# Revit family: WTC-OB25W-RU20
name_source: partatom
category: HLS-Bauteile
revit_build: Autodesk Revit 2017 (Build: 20160225_1515(x64)
units: mm (PartAtom-declared; Revit-internal decimal feet)

## family parameters
Arbeitsebenenbasiert = Nein
Beim Laden mit Abzugskörper schneiden = Nein
Bemaßung runder Anschluss = Durchmesser verwenden
Gemeinsam genutzt = Nein
Immer vertikal = Ja
Raumberechnungspunkt = Nein
Teiletyp = Normal

## types (1)
- Thermo Condens, WTC-OB 25-A W-PEA, 24.3 kW
    Anordnung, Lage = nebenstehend
    Baugruppenkennzeichen = ????
    Beschreibung = Weishaupt Thermo Condens Ölbrennwert Typ WTC-OB 25-A Ausf. W-PEA
    Bestellnummer = 46211201
    Brennstoffart = flüssige Brennstoffe
    Datanorm Nummer = 46211201
    Generiert am = 06.02.2018
    Generiert durch = Rubicon Professional Solutions GmbH
    Hersteller = MAX WEISHAUPT GMBH
    Herstellerkurzname = Weishaupt
    Modell = Thermo Condens WTC-OB 25-A W-PEA
    Name der Richtlinie = Wärmeerzeuger
    Produktgruppe = Brennwert-Kessel
    Quelle = http://www.vdi3805-portal.de
    Revisionsdatum der VDI-Datei = 09.10.2017
    Stand der Richtlinie = 01.06.2004
    TGA-Nr = 00100100000400000000100000000400200000000000002531???00001000010000100000000000000000001
    Trinkwasserprinzip = Speicher extern
    Typenbezeichnung (Name) = Thermo Condens, WTC-OB 25-A W-PEA, 24.3 kW
    Typenkommentare = Die Daten geben den Stand des eingeblendeten Datums wieder. Fuer Vollstaendigkeit und Richtigkeit kann keine Gewaehr uebernommen werden!
    URL = http://www.weishaupt.de
    VDI3805-Richtlinienblatt = 3
    Web-Adresse = http://www.vdi3805-portal.de
    WebService = http://www.vdi3805-portal.de
    Werkstoff = Aluminium
    XML = <?xml version="1.0"?>
<pData xmlns="http://www.rubicon-professional.de xmlns:xsi="http://www.w3.org filename="PART03_Weishaupt.VDI" shortname="Weishaupt" manufacturername="MAX WEISHAUPT GMBH" tganr="00100100000400000000100000000400200000000000002531???00001000010000100000000000000000001|" language="de-DE"/><REC010 IDX="010" index="3" content="010;3;200406;MAX WEISHAUPT GMBH;20171009;http://www.weishaupt.de;Die Daten geben den Stand des eingeblendeten Datums wieder. Fuer Vollstaendigkeit und Richtigkeit kann keine Gewaehr uebernommen werden!;1234567890123;;;1;20170801;DEU;DE;201110;"><RECORDS_100><REC100 IDX="100" index="1" content="100;1;1;Bodenstehender Waermeerzeuger, nur fuer Heizung;;;20071101;"><RECORDS_110><REC110 IDX="110" index="1" content="110;1;1;mit Geblaese;;;20071101;"><RECORDS_200><REC200 IDX="200" index="4" content="200;4;Aluminium;"/></RECORDS_200><RECORDS_300><REC300 IDX="300" index="1" content="300;1;fluessige Brennstoffe;"/></RECORDS_300><RECORDS_400><REC400 IDX="400" index="4" content="400;4;Speicher extern;"><RECORDS_450><REC450 IDX="450" index="2" content="450;2;nebenstehend;"/></RECORDS_450></REC400></RECORDS_400><RECORDS_700><REC700 IDX="700" index="2531" content="700;2531;23;Thermo Condens;WTC-OB 25-A W-PEA;24.3;140;23;;;;;15.4;3;Brennwert-Kessel;1;2-Zug-Kessel;1.1;3;raumluftabhaengig oder -unabhaengig;1;1;80;125;;;96.2;0.004;0.156;24.3;"><RECORDS_710_01><REC71001 IDX="710.01" index="1" content="710.01;1;40/30;15.8;25.9;105;98;102;85;0;33;;85;;;;;;3;;100;0;;;24;215;1;7;90;17330;63;"><RECORDS_710_11><REC71011 IDX="710.11" index="1" content="710.11;1;1;9;Heizoel EL;"/></RECORDS_710_11></REC71001></RECORDS_710_01><RECORDS_710_05><REC71005 IDX="710.05" index="1" content="710.05;1;2;zweistufig;0.0107;0.0062;;56;54;;13;13;100;10;;;6;Klasse 3/EN 676;;purflam-Oelbrenner;;25.2;"/></RECORDS_710_05><RECORDS_710_10><REC71010 IDX="710.10" index="1" content="710.10;1;2;730;680;1182;Geraetemass;"/><REC71010 IDX="710.10" index="2" content="710.10;2;2;1250;680;1182;Platzbedarf fuer Wartung;"/></RECORDS_710_10><RECORDS_710_12><REC71012 IDX="710.12" index="1" content="710.12;1;6;Aussenfuehler mit modulierendem Volumenstrom;4;1;1;0;1;1;7;0;1;1;1;1;1;Weishaupt Condens Manager WCM;;4;0;"/></RECORDS_710_12><RECORDS_720><REC720 IDX="720" index="1" content="720;1;46201102;"/></RECORDS_720><RECORDS_740><REC740 IDX="740" index="1" content="740;1;CE-PIN;0036 0392/10;"/><REC740 IDX="740" index="2" content="740;2;DIN-CERTCO-Nr.;3R279/11;"/><REC740 IDX="740" index="3" content="740;3;VKF-Nr.;22349;"/></RECORDS_740><RECORDS_760><REC760 IDX="760" index="1" content="760;1;Geraete-Anschluss-Zubehoer;"/><REC760 IDX="760" index="3" content="760;3;Hydraulik-Zubehoer;"/><REC760 IDX="760" index="4" content="760;4;Hydraulik-Zubehoer Trinkwasser;"/><REC760 IDX="760" index="19" content="760;19;Energiespeicher;"/><REC760 IDX="760" index="9" content="760;9;Trinkwasserspeicher;"/></RECORDS_760></REC700></RECORDS_700></REC110></RECORDS_110></REC100></RECORDS_100><RECORDS_970><REC970 IDX="970" index="520" content="970;520;WTC-OB 20/25/30/35 A (RFER);0;QUAD;0;0;0;1;0;0;0;1;0;1;1;1;0;0;0;0;0;0;0;0;"><RECORDS_970_02><REC97002 IDX="970.02" index="1" content="970.02;1;G;ZYLI;-310;-20;0;0;0;1;0;1;0;15;16;0;0;0;0;0;0;0;0;4;"/><REC97002 IDX="970.02" index="2" content="970.02;2;G;ZYLI;310;-20;0;0;0;1;0;1;0;15;16;0;0;0;0;0;0;0;0;4;"/><REC97002 IDX="970.02" index="5" content="970.02;5;G;WIED;0;-557;0;1;0;0;0;1;0;1;0;0;0;0;0;0;0;0;0;0;1;2;"/><REC97002 IDX="970.02" index="10" content="970.02;10;G;QUAD;-330;-610;15;1;0;0;0;1;0;660;610;35;0;0;0;0;0;0;0;4;"/><REC97002 IDX="970.02" index="15" content="970.02;15;G;QUAD;-340;-730;50;1;0;0;0;1;0;680;730;1021.5;0;0;0;0;0;0;0;1;"/><REC97002 IDX="970.02" index="16" content="970.02;16;G;TRAN;-340;-730;1071.5;0;1;0;0;0;1;0;0;1;680;100;0;0;0;0;0;8;"/><REC97002 IDX="970.02" index="17" content="970.02;17;G;TRAN;-340;-730;1071.5;0;1;0;0;0;1;0;0;1;680;200;0;0;0;0;0;1;"/><REC97002 IDX="970.02" index="23" content="970.02;23;G;ZYLI;0;-50;1201.5;0;0;1;0;1;0;25.5;13.5;0;0;0;0;0;0;0;0;3;"/><REC97002 IDX="970.02" index="27" content="970.02;27;G;ZYLI;280;-50;1201.5;0;0;1;0;1;0;23.5;6;0;0;0;0;0;0;0;0;5;"/><REC97002 IDX="970.02" index="50" content="970.02;50;G;ZYLI;-262;-84;1201.5;0;0;1;-1;0;0;23.5;24;0;0;0;0;0;0;0;0;3;"/><REC97002 IDX="970.02" index="51" content="970.02;51;G;ZYLI;-137;-84;1201.5;0;0;1;-1;0;0;23.5;24;0;0;0;0;0;0;0;0;3;"/><REC97002 IDX="970.02" index="62" content="970.02;62;G;ZYLI;181;-162;1201.5;0;0;1;0;-1;0;18.5;62.5;0;0;0;0;0;0;0;0;3;"/><REC97002 IDX="970.02" index="90" content="970.02;90;G;QUAD;175;-732;1100;1;0;0;0;1;0;125;2;25;0;0;0;0;0;0;0;3;"/><REC97002 IDX="970.02" index="100" content="970.02;100;D;STRE;0;0;0;1;0;0;0;1;0;101;0;0;100;0;0;0;0;0;0;0;"/><REC97002 IDX="970.02" index="101" content="970.02;101;D;STRE;0;0;0;1;0;0;0;1;0;102;100;0;200;130;0;0;0;0;0;0;"/><REC97002 IDX="970.02" index="102" content="970.02;102;D;STRE;0;0;0;1;0;0;0;1;0;103;200;130;0;130;0;0;0;0;0;0;"/><REC97002 IDX="970.02" index="103" content="970.02;103;D;STRE;0;0;0;1;0;0;0;1;0;100;0;130;0;0;0;0;0;0;0;0;"/><REC97002 IDX="970.02" index="200" content="970.02;200;D;STRE;0;0;0;1;0;0;0;1;0;201;100;0;200;130;0;0;0;0;0;0;"/><REC97002 IDX="970.02" index="201" content="970.02;201;D;STRE;0;0;0;1;0;0;0;1;0;202;200;130;730;130;0;0;0;0;0;0;"/><REC97002 IDX="970.02" index="202" content="970.02;202;D;STRE;0;0;0;1;0;0;0;1;0;203;730;130;730;0;0;0;0;0;0;0;"/><REC97002 IDX="970.02" index="203" content="970.02;203;D;STRE;0;0;0;1;0;0;0;1;0;200;730;0;100;0;0;0;0;0;0;0;"/></RECORDS_970_02><RECORDS_970_03><REC97003 IDX="970.03" index="1" content="970.03;1;G;ZYLI;-310;-20;0;0;0;1;0;1;0;8;16;0;0;0;0;0;0;0;0;4;"/><REC97003 IDX="970.03" index="2" content="970.03;2;G;VKNT;-310;-20;8;0;0;1;0;1;0;8;10;6;0;0;0;0;0;0;0;4;"/><REC97003 IDX="970.03" index="3" content="970.03;3;G;ZYLI;-310;-20;8;0;0;1;0;1;0;45;6;0;0;0;0;0;0;0;0;4;"/><REC97003 IDX="970.03" index="4" content="970.03;4;G;VKNT;-310;-20;23;0;0;1;0;1;0;8;10;6;0;0;0;0;0;0;0;4;"/><REC97003 IDX="970.03" index="5" content="970.03;5;G;WIED;0;-557;0;1;0;0;0;1;0;2;620;0;0;1;0;0;0;1;0;0;1;2;3;4;"/><REC97003 IDX="970.03" index="6" content="970.03;6;G;WIED;620;0;0;1;0;0;0;1;0;1;0;0;0;0;0;0;0;0;0;0;1;2;3;4;"/><REC97003 IDX="970.03" index="7" content="970.03;7;G;TRAN;-330;-602;23;1;0;0;0;0;-1;0;0;1;597;820;0;0;0;0;0;4;"/><REC97003 IDX="970.03" index="8" content="970.03;8;G;TRAN;-327;-8;23;1;0;0;0;1;0;0;0;1;1048.5;800;0;0;0;0;0;4;"/><REC97003 IDX="970.03" index="9" content="970.03;9;G;TRAN;-297;-602;1071.5;-1;0;0;0;0;1;0;0;1;597;800;0;0;0;0;0;4;"/><REC97003 IDX="970.03" index="10" content="970.03;10;G;TRAN;-327;-597;23;0;1;0;-1;0;0;0;0;1;1048.5;800;0;0;0;0;0;4;"/><REC97003 IDX="970.03" index="11" content="970.03;11;G;TRAN;330;-5;23;-1;0;0;0;0;-1;0;0;1;597;820;0;0;0;0;0;4;"/><REC97003 IDX="970.03" index="12" content="970.03;12;G;TRAN;297;-5;1071.5;1;0;0;0;0;1;0;0;1;597;800;0;0;0;0;0;4;"/><REC97003 IDX="970.03" index="13" content="970.03;13;G;TRAN;327;-8;23;0;-1;0;1;0;0;0;0;1;1048.5;800;0;0;0;0;0;4;"/><REC97003 IDX="970.03" index="14" content="970.03;14;G;TRAN;327;-597;23;-1;0;0;0;-1;0;0;0;1;1048.5;800;0;0;0;0;0;4;"/><REC97003 IDX="970.03" index="15" content="970.03;15;G;RURO;280;-30;820;0;1;0;-1;0;0;10;25;20;0;0;0;0;0;0;0;3;"/><REC97003 IDX="970.03" index="16" content="970.03;16;G;RURO;-280;-30;820;0;1;0;-1;0;0;10;25;20;0;0;0;0;0;0;0;3;"/><REC97003 IDX="970.03" index="17" content="970.03;17;G;TRAN;327;-11;247;0;-1;0;0;0;1;0;0;1;654;800;0;0;0;0;0;3;"/><REC97003 IDX="970.03" index="18" content="970.03;18;G;TRAN;327;-594;217;0;0;-1;0;-1;0;0;0;1;654;800;0;0;0;0;0;3;"/><REC97003 IDX="970.03" index="20" content="970.03;20;G;QUAD;-310;-5;230;1;0;0;0;1;0;620;3;836.5;0;0;0;0;0;0;0;4;1118;1119;"/><REC97003 IDX="970.03" index="23" content="970.03;23;G;RURO;0;-50;1202.5;0;0;1;0;1;0;2;20;13.5;0;0;0;0;0;0;0;3;"/><REC97003 IDX="970.03" index="24" content="970.03;24;G;VKNT;0;-50;1222.5;0;0;1;0;1;0;15;17;6;0;0;0;0;0;0;0;3;1121;"/><REC97003 IDX="970.03" index="26" content="970.03;26;G;ZYLI;0;-50;1201.5;0;0;1;0;1;0;2;20;0;0;0;0;0;0;0;0;8;"/><REC97003 IDX="970.03" index="27" content="970.03;27;G;RURO;280;-50;1170;0;0;1;0;1;0;1;40;6;0;0;0;0;0;0;0;5;"/><REC97003 IDX="970.03" index="28" content="970.03;28;G;VKNT;280;-50;1210;0;0;1;0;1;0;15;9;6;0;0;0;0;0;0;0;5;1120;"/><REC97003 IDX="970.03" index="29" content="970.03;29;G;RURO;280;-50;1201.5;0;0;1;0;1;0;6;2;12;0;0;0;0;0;0;0;8;"/><REC97003 IDX="970.03" index="30" content="970.03;30;G;QUAD;335;-5;50;0;1;0;-1;0;0;5;30;1016.5;0;0;0;0;0;0;0;1;"/><REC97003 IDX="970.03" index="31" content="970.03;31;G;QUAD;-335;0;50;0;-1;0;1;0;0;5;25;1016.5;0;0;0;0;0;0;0;1;"/><REC97003 IDX="970.03" index="32" content="970.03;32;G;QUAD;-330;-720;50;1;0;0;0;1;0;660;118;5;0;0;0;0;0;0;0;1;"/><REC97003 IDX="970.03" index="33" content="970.03;33;G;TRAN;0;-730;50;1;0;0;0;1;0;0;0;1;1016.5;100;0;0;0;0;0;1;"/><REC97003 IDX="970.03" index="36" content="970.03;36;G;TRAN;-340;-730;1071.5;1;0;0;0;1;0;0;0;1;125;230;0;0;0;0;0;8;1000;"/><REC97003 IDX="970.03" index="37" content="970.03;37;G;TRAN;340;-730;1196.5;-1;0;0;0;1;0;0;0;1;125;230;0;0;0;0;0;8;1000;"/><REC97003 IDX="970.03" index="38" content="970.03;38;G;TRAN;-335;-730;1196.5;0;1;0;0;0;1;0;0;1;670;250;0;0;0;0;0;8;1000;1002;1003;1004;1005;1006;"/><REC97003 IDX="970.03" index="39" content="970.03;39;G;ROTA;335;-730;1196.5;0;-1;0;1;0;0;1;0;0;0;0;0;90;200;0;0;8;1000;"/><REC97003 IDX="970.03" index="40" content="970.03;40;G;ROTA;-335;-730;1196.5;0;-1;0;0;0;1;1;0;0;0;0;0;90;200;0;0;8;1000;"/><REC97003 IDX="970.03" index="41" content="970.03;41;G;TRAN;0;-162;1201.5;1;0;0;0;0;1;0;0;1;440;300;0;0;0;0;0;1;1010;1102;"/><REC97003 IDX="970.03" index="42" content="970.03;42;G;QUAD;335;-15;1071.5;0;0;1;0;1;0;125;15;670;0;0;0;0;0;0;0;1;"/><REC97003 IDX="970.03" index="43" content="970.03;43;G;TRAN;-139;-730;1071.5;0;1;0;0;0;1;0;0;1;278;280;0;0;0;0;0;8;"/><REC97003 IDX="970.03" index="45" content="970.03;45;G;QUAD;-330;-715;1071.5;0;1;0;1;0;0;115;5;10;0;0;0;0;0;0;0;8;"/><REC97003 IDX="970.03" index="46" content="970.03;46;G;QUAD;325;-715;1071.5;0;1;0;1;0;0;115;5;10;0;0;0;0;0;0;0;8;"/><REC97003 IDX="970.03" index="47" content="970.03;47;G;QUAD;-330;-715;1071.5;1;0;0;0;-1;0;660;5;10;0;0;0;0;0;0;0;8;"/><REC97003 IDX="970.03" index="48" content="970.03;48;G;QUAD;327;-597;23;-1;0;0;0;0;1;650;30;3;0;0;0;0;0;0;0;3;"/><REC97003 IDX="970.03" index="49" content="970.03;49;G;QUAD;327;-200;23;-1;0;0;0;-1;0;650;30;3;0;0;0;0;0;0;0;3;"/><REC97003 IDX="970.03" index="50" content="970.03;50;G;RURO;-262;-84;1116;0;0;1;-1;0;0;2.6;105;24;0;0;0;0;0;0;0;3;"/><REC97003 IDX="970.03" index="51" content="970.03;51;G;RURO;-262;-84;1220;0;0;1;-1;0;0;5;5;26;0;0;0;0;0;0;0;3;"/><REC97003 IDX="970.03" index="52" content="970.03;52;G;VKNT;-262;-84;1220;0;0;1;-1;0;0;25;30;6;0;0;0;0;0;0;0;3;1115;"/><REC97003 IDX="970.03" index="53" content="970.03;53;G;RURO;-262;-84;1201.5;0;0;1;-1;0;0;11;2;35;0;0;0;0;0;0;0;8;"/><REC97003 IDX="970.03" index="55" content="970.03;55;G;WIED;125;0;0;1;0;0;0;1;0;1;0;0;0;0;0;0;0;0;0;0;50;51;52;53;"/><REC97003 IDX="970.03" index="58" content="970.03;58;G;TRAN;0;0;1201.5;1;0;0;0;0;1;0;0;1;260;300;0;0;0;0;0;1;1116;1103;1007;1008;1009;"/><REC97003 IDX="970.03" index="62" content="970.03;62;G;RURO;181;-162;1096.5;0;0;1;0;-1;0;2;100;64.5;0;0;0;0;0;0;0;3;"/><REC97003 IDX="970.03" index="70" content="970.03;70;G;TRAN;0;-50;35;1;0;0;0;0;1;0;0;1;500;400;0;0;0;0;0;8;"/><REC97003 IDX="970.03" index="75" content="970.03;75;G;ROTA;181;-162;1099.5;-1;0;0;0;0;1;0;1;0;0;0;0;360;600;0;0;3;"/><REC97003 IDX="970.03" index="88" content="970.03;88;G;QUAD;300;-30;250;0;0;1;-1;0;0;880;600;550;0;0;0;0;0;0;0;3;"/><REC97003 IDX="970.03" index="90" content="970.03;90;G;QUAD;175;-732;1100;1;0;0;0;1;0;125;2;25;0;0;0;0;0;0;0;3;"/><REC97003 IDX="970.03" index="100" content="970.03;100;D;STRE;0;0;0;1;0;0;0;1;0;101;-335;0;335;0;0;0;0;0;0;0;"/><REC97003 IDX="970.03" index="101" content="970.03;101;D;BOGN;0;0;0;1;0;0;0;1;0;102;335;0;340;5;5;335;5;0;0;0;"/><REC97003 IDX="970.03" index="102" content="970.03;102;D;STRE;0;0;0;1;0;0;0;1;0;103;340;5;340;128;0;0;0;0;0;0;"/><REC97003 IDX="970.03" index="103" content="970.03;103;D;STRE;0;0;0;1;0;0;0;1;0;104;340;128;335;128;0;0;0;0;0;0;"/><REC97003 IDX="970.03" index="104" content="970.03;104;D;STRE;0;0;0;1;0;0;0;1;0;105;335;128;335;130;0;0;0;0;0;0;"/><REC97003 IDX="970.03" index="105" content="970.03;105;D;STRE;0;0;0;1;0;0;0;1;0;106;335;130;330;130;0;0;0;0;0;0;"/><REC97003 IDX="970.03" index="106" content="970.03;106;D;STRE;0;0;0;1;0;0;0;1;0;107;330;130;330;10;0;0;0;0;0;0;"/><REC97003 IDX="970.03" index="107" content="970.03;107;D;STRE;0;0;0;1;0;0;0;1;0;108;330;10;-330;10;0;0;0;0;0;0;"/><REC97003 IDX="970.03" index="108" content="970.03;108;D;STRE;0;0;0;1;0;0;0;1;0;109;-330;10;-330;130;0;0;0;0;0;0;"/><REC97003 IDX="970.03" index="109" content="970.03;109;D;STRE;0;0;0;1;0;0;0;1;0;110;-330;130;-335;130;0;0;0;0;0;0;"/><REC97003 IDX="970.03" index="110" content="970.03;110;D;STRE;0;0;0;1;0;0;0;1;0;111;-335;130;-335;128;0;0;0;0;0;0;"/><REC97003 IDX="970.03" index="111" content="970.03;111;D;STRE;0;0;0;1;0;0;0;1;0;112;-335;128;-340;128;0;0;0;0;0;0;"/><REC97003 IDX="970.03" index="112" content="970.03;112;D;STRE;0;0;0;1;0;0;0;1;0;113;-340;128;-340;5;0;0;0;0;0;0;"/><REC97003 IDX="970.03" index="113" content="970.03;113;D;BOGN;0;0;0;1;0;0;0;1;0;100;-340;5;-335;0;5;-335;5;0;0;0;"/><REC97003 IDX="970.03" index="200" content="970.03;200;D;STRE;0;0;0;1;0;0;0;1;0;201;-245;0;0;0;0;0;0;0;0;0;"/><REC97003 IDX="970.03" index="201" content="970.03;201;D;BOGN;0;0;0;1;0;0;0;1;0;202;0;0;-5;5;5;-5;0;0;0;0;"/><REC97003 IDX="970.03" index="202" content="970.03;202;D;STRE;0;0;0;1;0;0;0;1;0;203;-5;5;-245;5;0;0;0;0;0;0;"/><REC97003 IDX="970.03" index="203" content="970.03;203;D;STRE;0;0;0;1;0;0;0;1;0;200;-245;5;-245;0;0;0;0;0;0;0;"/><REC97003 IDX="970.03" index="230" content="970.03;230;D;STRE;0;0;0;1;0;0;0;1;0;231;0;240;0;5;0;0;0;0;0;0;"/><REC97003 IDX="970.03" index="231" content="970.03;231;D;BOGN;0;0;0;1;0;0;0;1;0;232;0;5;5;0;5;5;5;0;0;0;"/><REC97003 IDX="970.03" index="232" content="970.03;232;D;STRE;0;0;0;1;0;0;0;1;0;233;5;0;200;0;0;0;0;0;0;0;"/><REC97003 IDX="970.03" index="233" content="970.03;233;D;STRE;0;0;0;1;0;0;0;1;0;234;200;0;200;5;0;0;0;0;0;0;"/><REC97003 IDX="970.03" index="234" content="970.03;234;D;STRE;0;0;0;1;0;0;0;1;0;235;200;5;205;5;0;0;0;0;0;0;"/><REC97003 IDX="970.03" index="235" content="970.03;235;D;STRE;0;0;0;1;0;0;0;1;0;236;205;5;205;240;0;0;0;0;0;0;"/><REC97003 IDX="970.03" index="236" content="970.03;236;D;STRE;0;0;0;1;0;0;0;1;0;230;205;240;0;240;0;0;0;0;0;0;"/><REC97003 IDX="970.03" index="250" content="970.03;250;D;STRE;0;0;0;1;0;0;0;1;0;251;0;0;245;0;0;0;0;0;0;0;"/><REC97003 IDX="970.03" index="251" content="970.03;251;D;STRE;0;0;0;1;0;0;0;1;0;252;245;0;245;5;0;0;0;0;0;0;"/><REC97003 IDX="970.03" index="252" content="970.03;252;D;STRE;0;0;0;1;0;0;0;1;0;253;245;5;5;5;0;0;0;0;0;0;"/><REC97003 IDX="970.03" index="253" content="970.03;253;D;BOGN;0;0;0;1;0;0;0;1;0;250;5;5;0;0;5;5;0;0;0;0;"/><REC97003 IDX="970.03" index="280" content="970.03;280;D;STRE;0;0;0;1;0;0;0;1;0;281;0;0;5;0;0;0;0;0;0;0;"/><REC97003 IDX="970.03" index="281" content="970.03;281;D;STRE;0;0;0;1;0;0;0;1;0;282;5;0;5;125;0;0;0;0;0;0;"/><REC97003 IDX="970.03" index="282" content="970.03;282;D;STRE;0;0;0;1;0;0;0;1;0;283;5;125;152;125;0;0;0;0;0;0;"/><REC97003 IDX="970.03" index="283" content="970.03;283;D;STRE;0;0;0;1;0;0;0;1;0;284;152;125;152;130;0;0;0;0;0;0;"/><REC97003 IDX="970.03" index="284" content="970.03;284;D;STRE;0;0;0;1;0;0;0;1;0;285;152;130;5;130;0;0;0;0;0;0;"/><REC97003 IDX="970.03" index="285" content="970.03;285;D;BOGN;0;0;0;1;0;0;0;1;0;286;5;130;0;125;5;5;125;0;0;0;"/><REC97003 IDX="970.03" index="286" content="970.03;286;D;STRE;0;0;0;1;0;0;0;1;0;280;0;125;0;0;0;0;0;0;0;0;"/><REC97003 IDX="970.03" index="300" content="970.03;300;D;STRE;0;0;0;1;0;0;0;1;0;301;335;0;-335;0;0;0;0;0;0;0;"/><REC97003 IDX="970.03" index="301" content="970.03;301;D;BOGN;0;0;0;1;0;0;0;1;0;302;-335;0;-340;-5;5;-335;-5;0;0;0;"/><REC97003 IDX="970.03" index="302" content="970.03;302;D;STRE;0;0;0;1;0;0;0;1;0;303;-340;-5;-340;-130;0;0;0;0;0;0;"/><REC97003 IDX="970.03" index="303" content="970.03;303;D;STRE;0;0;0;1;0;0;0;1;0;304;-340;-130;-335;-130;0;0;0;0;0;0;"/><REC97003 IDX="970.03" index="304" content="970.03;304;D;STRE;0;0;0;1;0;0;0;1;0;305;-335;-130;-335;-5;0;0;0;0;0;0;"/><REC97003 IDX="970.03" index="305" content="970.03;305;D;STRE;0;0;0;1;0;0;0;1;0;306;-335;-5;335;-5;0;0;0;0;0;0;"/><REC97003 IDX="970.03" index="306" content="970.03;306;D;STRE;0;0;0;1;0;0;0;1;0;307;335;-5;335;-130;0;0;0;0;0;0;"/><REC97003 IDX="970.03" index="307" content="970.03;307;D;STRE;0;0;0;1;0;0;0;1;0;308;335;-130;340;-130;0;0;0;0;0;0;"/><REC97003 IDX="970.03" index="308" content="970.03;308;D;STRE;0;0;0;1;0;0;0;1;0;309;340;-130;340;-5;0;0;0;0;0;0;"/><REC97003 IDX="970.03" index="309" content="970.03;309;D;BOGN;0;0;0;1;0;0;0;1;0;300;340;-5;335;0;5;335;-5;0;0;0;"/><REC97003 IDX="970.03" index="400" content="970.03;400;D;STRE;0;0;0;1;0;0;0;1;0;401;-290;0;290;0;0;0;0;0;0;0;"/><REC97003 IDX="970.03" index="401" content="970.03;401;D;BOGN;0;0;0;1;0;0;0;1;0;402;290;0;300;8;10;290.20162629;9.99796714;0;0;0;"/><REC97003 IDX="970.03" index="402" content="970.03;402;D;STRE;0;0;0;1;0;0;0;1;0;403;300;8;305;20;0;0;0;0;0;0;"/><REC97003 IDX="970.03" index="403" content="970.03;403;D;STRE;0;0;0;1;0;0;0;1;0;404;305;20;320;20;0;0;0;0;0;0;"/><REC97003 IDX="970.03" index="404" content="970.03;404;D;STRE;0;0;0;1;0;0;0;1;0;405;320;20;320;25;0;0;0;0;0;0;"/><REC97003 IDX="970.03" index="405" content="970.03;405;D;STRE;0;0;0;1;0;0;0;1;0;406;320;25;300;25;0;0;0;0;0;0;"/><REC97003 IDX="970.03" index="406" content="970.03;406;D;STRE;0;0;0;1;0;0;0;1;0;407;300;25;295;10;0;0;0;0;0;0;"/><REC97003 IDX="970.03" index="407" content="970.03;407;D;BOGN;0;0;0;1;0;0;0;1;0;408;290;5;295;10;5;290;10;0;0;0;"/><REC97003 IDX="970.03" index="408" content="970.03;408;D;STRE;0;0;0;1;0;0;0;1;0;409;290;5;-290;5;0;0;0;0;0;0;"/><REC97003 IDX="970.03" index="409" content="970.03;409;D;BOGN;0;0;0;1;0;0;0;1;0;410;-295;10;-290;5;5;-290;10;0;0;0;"/><REC97003 IDX="970.03" index="410" content="970.03;410;D;STRE;0;0;0;1;0;0;0;1;0;411;-295;10;-300;25;0;0;0;0;0;0;"/><REC97003 IDX="970.03" index="411" content="970.03;411;D;STRE;0;0;0;1;0;0;0;1;0;412;-300;25;-320;25;0;0;0;0;0;0;"/><REC97003 IDX="970.03" index="412" content="970.03;412;D;STRE;0;0;0;1;0;0;0;1;0;413;-320;25;-320;20;0;0;0;0;0;0;"/><REC97003 IDX="970.03" index="413" content="970.03;413;D;STRE;0;0;0;1;0;0;0;1;0;414;-320;20;-305;20;0;0;0;0;0;0;"/><REC97003 IDX="970.03" index="414" content="970.03;414;D;STRE;0;0;0;1;0;0;0;1;0;415;-305;20;-300;8;0;0;0;0;0;0;"/><REC97003 IDX="970.03" index="415" content="970.03;415;D;BOGN;0;0;0;1;0;0;0;1;0;400;-300;8;-290;0;10;-290.20162629;9.99796714;0;0;0;"/><REC97003 IDX="970.03" index="600" content="970.03;600;D;STRE;0;0;0;1;0;0;0;1;0;601;40;0;40;50;0;0;0;0;0;0;"/><REC97003 IDX="970.03" index="601" content="970.03;601;D;STRE;0;0;0;1;0;0;0;1;0;602;40;50;45;55;0;0;0;0;0;0;"/><REC97003 IDX="970.03" index="602" content="970.03;602;D;STRE;0;0;0;1;0;0;0;1;0;603;45;55;45;100;0;0;0;0;0;0;"/><REC97003 IDX="970.03" index="603" content="970.03;603;D;STRE;0;0;0;1;0;0;0;1;0;604;45;100;50;100;0;0;0;0;0;0;"/><REC97003 IDX="970.03" index="604" content="970.03;604;D;STRE;0;0;0;1;0;0;0;1;0;605;50;100;50;110;0;0;0;0;0;0;"/><REC97003 IDX="970.03" index="605" content="970.03;605;D;STRE;0;0;0;1;0;0;0;1;0;606;50;110;45;110;0;0;0;0;0;0;"/><REC97003 IDX="970.03" index="606" content="970.03;606;D;STRE;0;0;0;1;0;0;0;1;0;607;45;110;45;115;0;0;0;0;0;0;"/><REC97003 IDX="970.03" index="607" content="970.03;607;D;STRE;0;0;0;1;0;0;0;1;0;608;45;115;43;115;0;0;0;0;0;0;"/><REC97003 IDX="970.03" index="608" content="970.03;608;D;STRE;0;0;0;1;0;0;0;1;0;609;43;115;43;108;0;0;0;0;0;0;"/><REC97003 IDX="970.03" index="609" content="970.03;609;D;STRE;0;0;0;1;0;0;0;1;0;610;43;108;48;108;0;0;0;0;0;0;"/><REC97003 IDX="970.03" index="610" content="970.03;610;D;STRE;0;0;0;1;0;0;0;1;0;611;48;108;48;102;0;0;0;0;0;0;"/><REC97003 IDX="970.03" index="611" content="970.03;611;D;STRE;0;0;0;1;0;0;0;1;0;612;48;102;43;102;0;0;0;0;0;0;"/><REC97003 IDX="970.03" index="612" content="970.03;612;D;STRE;0;0;0;1;0;0;0;1;0;613;43;102;43;56;0;0;0;0;0;0;"/><REC97003 IDX="970.03" index="613" content="970.03;613;D;STRE;0;0;0;1;0;0;0;1;0;614;43;56;38;51;0;0;0;0;0;0;"/><REC97003 IDX="970.03" index="614" content="970.03;614;D;STRE;0;0;0;1;0;0;0;1;0;615;38;51;38;0;0;0;0;0;0;0;"/><REC97003 IDX="970.03" index="615" content="970.03;615;D;STRE;0;0;0;1;0;0;0;1;0;600;38;0;40;0;0;0;0;0;0;0;"/><REC97003 IDX="970.03" index="700" content="970.03;700;D;STRE;0;0;0;1;0;0;0;1;0;701;0;350;0;266;0;0;0;0;0;0;"/><REC97003 IDX="970.03" index="701" content="970.03;701;D;BOGN;0;0;0;1;0;0;0;1;0;702;0;266;0;96;85;0;181;0;0;0;"/><REC97003 IDX="970.03" index="702" content="970.03;702;D;STRE;0;0;0;1;0;0;0;1;0;703;0;96;0;-350;0;0;0;0;0;0;"/><REC97003 IDX="970.03" index="703" content="970.03;703;D;STRE;0;0;0;1;0;0;0;1;0;704;0;-350;-100;-350;0;0;0;0;0;0;"/><REC97003 IDX="970.03" index="704" content="970.03;704;D;STRE;0;0;0;1;0;0;0;1;0;705;-100;-350;-100;350;0;0;0;0;0;0;"/><REC97003 IDX="970.03" index="705" content="970.03;705;D;STRE;0;0;0;1;0;0;0;1;0;700;-100;350;0;350;0;0;0;0;0;0;"/><REC97003 IDX="970.03" index="800" content="970.03;800;D;STRE;0;0;0;1;0;0;0;1;0;801;0;0;0;-20;0;0;0;0;0;0;"/><REC97003 IDX="970.03" index="801" content="970.03;801;D;STRE;0;0;0;1;0;0;0;1;0;802;0;-20;-3;-20;0;0;0;0;0;0;"/><REC97003 IDX="970.03" index="802" content="970.03;802;D;STRE;0;0;0;1;0;0;0;1;0;803;-3;-20;-3;0;0;0;0;0;0;0;"/><REC97003 IDX="970.03" index="803" content="970.03;803;D;BOGN;0;0;0;1;0;0;0;1;0;804;0;3;-3;0;3;0;0;0;0;0;"/><REC97003 IDX="970.03" index="804" content="970.03;804;D;STRE;0;0;0;1;0;0;0;1;0;805;0;3;20;3;0;0;0;0;0;0;"/><REC97003 IDX="970.03" index="805" content="970.03;805;D;STRE;0;0;0;1;0;0;0;1;0;806;20;3;20;0;0;0;0;0;0;0;"/><REC97003 IDX="970.03" index="806" content="970.03;806;D;STRE;0;0;0;1;0;0;0;1;0;800;20;0;0;0;0;0;0;0;0;0;"/><REC97003 IDX="970.03" index="820" content="970.03;820;D;STRE;0;0;0;1;0;0;0;1;0;821;0;0;0;-30;0;0;0;0;0;0;"/><REC97003 IDX="970.03" index="821" content="970.03;821;D;STRE;0;0;0;1;0;0;0;1;0;822;0;-30;-3;-30;0;0;0;0;0;0;"/><REC97003 IDX="970.03" index="822" content="970.03;822;D;STRE;0;0;0;1;0;0;0;1;0;823;-3;-30;-3;0;0;0;0;0;0;0;"/><REC97003 IDX="970.03" index="823" content="970.03;823;D;BOGN;0;0;0;1;0;0;0;1;0;824;0;3;-3;0;3;0;0;0;0;0;"/><REC97003 IDX="970.03" index="824" content="970.03;824;D;STRE;0;0;0;1;0;0;0;1;0;825;0;3;30;3;0;0;0;0;0;0;"/><REC97003 IDX="970.03" index="825" content="970.03;825;D;STRE;0;0;0;1;0;0;0;1;0;826;30;3;30;0;0;0;0;0;0;0;"/><REC97003 IDX="970.03" index="826" content="970.03;826;D;STRE;0;0;0;1;0;0;0;1;0;820;30;0;0;0;0;0;0;0;0;0;"/><REC97003 IDX="970.03" index="1000" content="970.03;1000;H;EBEN;-10;-602;1066.5;0;0.8660254;-0.5;-1;0;0;0;0;0;0;0;0;0;0;0;0;0;"/><REC97003 IDX="970.03" index="1002" content="970.03;1002;H;QUAD;-140;-737;1194.5;1;0;0;0;1;0;280;160;10;0;0;0;0;0;0;0;0;"/><REC97003 IDX="970.03" index="1003" content="970.03;1003;H;QUAD;-140;-567;1194.5;1;0;0;0;1;0;280;5;10;0;0;0;0;0;0;0;0;"/><REC97003 IDX="970.03" index="1004" content="970.03;1004;H;QUAD;-140;-557;1194.5;1;0;0;0;1;0;280;5;10;0;0;0;0;0;0;0;0;"/><REC97003 IDX="970.03" index="1005" content="970.03;1005;H;QUAD;-140;-547;1194.5;1;0;0;0;1;0;280;5;10;0;0;0;0;0;0;0;0;"/><REC97003 IDX="970.03" index="1006" content="970.03;1006;H;QUAD;-140;-537;1194.5;1;0;0;0;1;0;280;5;10;0;0;0;0;0;0;0;0;"/><REC97003 IDX="970.03" index="1007" content="970.03;1007;H;ZYLI;-262;-84;1190;0;0;1;-1;0;0;20;30;0;0;0;0;0;0;0;0;0;"/><REC97003 IDX="970.03" index="1008" content="970.03;1008;H;ZYLI;-137;-84;1190;0;0;1;-1;0;0;20;30;0;0;0;0;0;0;0;0;0;"/><REC97003 IDX="970.03" index="1009" content="970.03;1009;H;ZYLI;280;-50;1109;0;0;1;0;1;0;20;13;0;0;0;0;0;0;0;0;0;"/><REC97003 IDX="970.03" index="1010" content="970.03;1010;H;EBEN;10;-601;1066.5;0;-0.8660254;0.5;-1;0;0;0;0;0;0;0;0;0;0;0;0;0;"/><REC97003 IDX="970.03" index="1102" content="970.03;1102;H;ZYLI;181;-162;1210;0;0;-1;-1;0;0;15;86;0;0;0;0;0;0;0;0;0;"/><REC97003 IDX="970.03" index="1103" content="970.03;1103;H;ZYLI;181;-162;1210;0;0;-1;-1;0;0;15;62.5;0;0;0;0;0;0;0;0;0;"/><REC97003 IDX="970.03" index="1115" content="970.03;1115;H;ZYLI;-262;-84;1218;0;0;1;-1;0;0;30;26;0;0;0;0;0;0;0;0;0;"/><REC97003 IDX="970.03" index="1116" content="970.03;1116;H;TRAN;0;-161;1210;0;1;0;1;0;0;0;0;1;150;700;0;0;0;0;0;0;"/><REC97003 IDX="970.03" index="1118" content="970.03;1118;H;ZYLI;280;-10;820;0;1;0;-1;0;0;10;20;0;0;0;0;0;0;0;0;0;"/><REC97003 IDX="970.03" index="1119" content="970.03;1119;H;ZYLI;-280;-10;820;0;1;0;-1;0;0;10;20;0;0;0;0;0;0;0;0;0;"/><REC97003 IDX="970.03" index="1120" content="970.03;1120;H;ZYLI;280;-50;1208;0;0;1;0;1;0;20;7;0;0;0;0;0;0;0;0;0;"/><REC97003 IDX="970.03" index="1121" content="970.03;1121;H;ZYLI;0;-50;1220;0;0;1;0;1;0;20;13;0;0;0;0;0;0;0;0;0;"/></RECORDS_970_03><RECORDS_970_04><REC97004 IDX="970.04" index="1" content="970.04;1;0.867;0.871;0.831;1;0.867;0.871;0.831;1;0.867;0.871;0.831;1;64;0;0;0;1;"/><REC97004 IDX="970.04" index="3" content="970.04;3;0.5;0.5;0.4;1;0.502;0.502;0.502;1;0.6;0.6;0.2;1;64;0;0;0;1;"/><REC97004 IDX="970.04" index="4" content="970.04;4;0.8118;0.8118;0.8118;1;0.7451;0.7451;0.7451;1;0.8745;0.8745;0.8745;1;48;0;0;0;1;"/><REC97004 IDX="970.04" index="5" content="970.04;5;0.3;0.2;0.1;1;0.7412;0.5529;0;1;1;0.9;0.8;1;24;0;0;0;1;"/><REC97004 IDX="970.04" index="8" content="970.04;8;0.4;0.35;0.4;1;0.3098;0.3098;0.3098;1;0.9;0.9;1;1;120;0;0;0;1;"/><REC97004 IDX="970.04" index="9" content="970.04;9;0.4;0.35;0.4;1;0.3098;0.3098;0.3098;1;0.9;0.9;1;1;35;0;0;0;1;"/><REC97004 IDX="970.04" index="12" content="970.04;12;1;1;0;1;1;1;0;1;1;1;0;1;64;0;0;0;1;"/><REC97004 IDX="970.04" index="20" content="970.04;20;0.196;0.463;0.384;1;0;0.8;0.2;1;0.196;0.463;0.384;1;128;0;0;0;1;"/></RECORDS_970_04></REC970><REC970 IDX="970" index="2" content="970;2;logo (RFER);0;QUAD;0;0;0;1;0;0;0;1;0;1;1;1;0;0;0;0;0;0;0;0;"><RECORDS_970_02><REC97002 IDX="970.02" index="1000" content="970.02;1000;G;TEXT;-10;-10;0.5;1;0;0;0;1;0;- weishaupt -;105;15;1;0;0;0;0;0;0;2;"/></RECORDS_970_02><RECORDS_970_03><REC97003 IDX="970.03" index="1" content="970.03;1;G;QUAD;-10;-5.5;0;1;0;0;0;1;0;8;1;2;0;0;0;0;0;0;0;2;"/><REC97003 IDX="970.03" index="2" content="970.03;2;G;TRAN;0;0;0;1;0;0;0;1;0;0;0;1;2;100;0;0;0;0;0;2;"/><REC97003 IDX="970.03" index="3" content="970.03;3;G;TRAN;0;0;0;1;0;0;0;1;0;0;0;1;2;200;0;0;0;0;0;2;4;"/><REC97003 IDX="970.03" index="4" content="970.03;4;H;TRAN;0;0;-1;1;0;0;0;1;0;0;0;1;4;210;0;0;0;0;0;0;"/><REC97003 IDX="970.03" index="5" content="970.03;5;G;QUAD;23.5;-10;0;1;0;0;0;1;0;1.5;10;2;0;0;0;0;0;0;0;2;"/><REC97003 IDX="970.03" index="6" content="970.03;6;G;QUAD;23.5;1.5;0;1;0;0;0;1;0;1.5;1.5;2;0;0;0;0;0;0;0;2;"/><REC97003 IDX="970.03" index="7" content="970.03;7;G;TRAN;0;0;0;1;0;0;0;1;0;0;0;1;2;300;0;0;0;0;0;2;"/><REC97003 IDX="970.03" index="8" content="970.03;8;G;TRAN;0;0;0;1;0;0;0;1;0;0;0;1;2;400;0;0;0;0;0;2;"/><REC97003 IDX="970.03" index="9" content="970.03;9;G;TRAN;0;0;0;1;0;0;0;1;0;0;0;1;2;500;0;0;0;0;0;2;10;"/><REC97003 IDX="970.03" index="10" content="970.03;10;H;TRAN;0;0;-1;1;0;0;0;1;0;0;0;1;4;520;0;0;0;0;0;0;"/><REC97003 IDX="970.03" index="11" content="970.03;11;G;TRAN;0;0;0;1;0;0;0;1;0;0;0;1;2;600;0;0;0;0;0;2;"/><REC97003 IDX="970.03" index="12" content="970.03;12;G;TRAN;0;0;0;1;0;0;0;1;0;0;0;1;2;700;0;0;0;0;0;2;13;"/><REC97003 IDX="970.03" index="13" content="970.03;13;H;TRAN;0;0;-1;1;0;0;0;1;0;0;0;1;4;720;0;0;0;0;0;0;"/><REC97003 IDX="970.03" index="14" content="970.03;14;G;TRAN;0;0;0;1;0;0;0;1;0;0;0;1;2;800;0;0;0;0;0;2;"/><REC97003 IDX="970.03" index="15" content="970.03;15;G;QUAD;85;-5.5;0;1;0;0;0;1;0;8;1;2;0;0;0;0;0;0;0;2;"/><REC97003 IDX="970.03" index="100" content="970.03;100;D;STRE;0;0;0;1;0;0;0;1;0;101;0;0;2.5;-10;0;0;0;0;0;0;"/><REC97003 IDX="970.03" index="101" content="970.03;101;D;STRE;0;0;0;1;0;0;0;1;0;102;2.5;-10;4;-10;0;0;0;0;0;0;"/><REC97003 IDX="970.03" index="102" content="970.03;102;D;STRE;0;0;0;1;0;0;0;1;0;103;4;-10;6;-4;0;0;0;0;0;0;"/><REC97003 IDX="970.03" index="103" content="970.03;103;D;STRE;0;0;0;1;0;0;0;1;0;104;6;-4;8;-10;0;0;0;0;0;0;"/><REC97003 IDX="970.03" index="104" content="970.03;104;D;STRE;0;0;0;1;0;0;0;1;0;105;8;-10;9.5;-10;0;0;0;0;0;0;"/><REC97003 IDX="970.03" index="105" content="970.03;105;D;STRE;0;0;0;1;0;0;0;1;0;106;9.5;-10;12;0;0;0;0;0;0;0;"/><REC97003 IDX="970.03" index="106" content="970.03;106;D;STRE;0;0;0;1;0;0;0;1;0;107;12;0;10.5;0;0;0;0;0;0;0;"/><REC97003 IDX="970.03" index="107" content="970.03;107;D;STRE;0;0;0;1;0;0;0;1;0;108;10.5;0;8.75;-7;0;0;0;0;0;0;"/><REC97003 IDX="970.03" index="108" content="970.03;108;D;STRE;0;0;0;1;0;0;0;1;0;109;8.75;-7;7;0;0;0;0;0;0;0;"/><REC97003 IDX="970.03" index="109" content="970.03;109;D;STRE;0;0;0;1;0;0;0;1;0;110;7;0;5.5;0;0;0;0;0;0;0;"/><REC97003 IDX="970.03" index="110" content="970.03;110;D;STRE;0;0;0;1;0;0;0;1;0;111;5.5;0;3.5;-7;0;0;0;0;0;0;"/><REC97003 IDX="970.03" index="111" content="970.03;111;D;STRE;0;0;0;1;0;0;0;1;0;112;3.5;-7;1.5;0;0;0;0;0;0;0;"/><REC97003 IDX="970.03" index="112" content="970.03;112;D;STRE;0;0;0;1;0;0;0;1;0;100;1.5;0;0;0;0;0;0;0;0;0;"/><REC97003 IDX="970.03" index="200" content="970.03;200;D;BOGN;0;0;0;1;0;0;0;1;0;201;22;-5;21;-8;5;17;-5;0;0;0;"/><REC97003 IDX="970.03" index="201" content="970.03;201;D;STRE;0;0;0;1;0;0;0;1;0;202;22;-5;13.5;-5;0;0;0;0;0;0;"/><REC97003 IDX="970.03" index="202" content="970.03;202;D;BOGN;0;0;0;1;0;0;0;1;0;203;13.5;-5;20;-6.5;3.5;16.98849952;-4.71650207;0;0;0;"/><REC97003 IDX="970.03" index="203" content="970.03;203;D;STRE;0;0;0;1;0;0;0;1;0;200;20;-6.5;21;-8;0;0;0;0;0;0;"/><REC97003 IDX="970.03" index="210" content="970.03;210;D;STRE;0;0;0;1;0;0;0;1;0;211;14;-3.5;20;-3.5;0;0;0;0;0;0;"/><REC97003 IDX="970.03" index="211" content="970.03;211;D;BOGN;0;0;0;1;0;0;0;1;0;210;20;-3.5;14;-3.5;3.5;17;-5.30277564;0;0;0;"/><REC97003 IDX="970.03" index="300" content="970.03;300;D;BOGN;0;0;0;1;0;0;0;1;0;301;36;-2;27;-2;6;31.5;-5.96862697;0;0;0;"/><REC97003 IDX="970.03" index="301" content="970.03;301;D;BOGN;0;0;0;1;0;0;0;1;0;302;27;-2;28;-5;2.5;29.33711731;-2.88762756;0;0;0;"/><REC97003 IDX="970.03" index="302" content="970.03;302;D;BOGN;0;0;0;1;0;0;0;1;0;303;28;-5;32;-6;10;32.37325787;3.9930315;0;0;0;"/><REC97003 IDX="970.03" index="303" content="970.03;303;D;BOGN;0;0;0;1;0;0;0;1;0;304;34;-6.5;32;-6;4;32.06262256;-9.99950977;0;0;0;"/><REC97003 IDX="970.03" index="304" content="970.03;304;D;BOGN;0;0;0;1;0;0;0;1;0;305;34;-8;34;-6.5;1;33.33856217;-7.25;0;0;0;"/><REC97003 IDX="970.03" index="305" content="970.03;305;D;BOGN;0;0;0;1;0;0;0;1;0;307;28;-7;34;-8;6;31.85027817;-2.39833096;0;0;0;"/><REC97003 IDX="970.03" index="307" content="970.03;307;D;STRE;0;0;0;1;0;0;0;1;0;308;28;-7;27;-8;0;0;0;0;0;0;"/><REC97003 IDX="970.03" index="308" content="970.03;308;D;BOGN;0;0;0;1;0;0;0;1;0;309;27;-8;35.5;-8.5;6.5;31.53842617;-3.34675512;0;0;0;"/><REC97003 IDX="970.03" index="309" content="970.03;309;D;BOGN;0;0;0;1;0;0;0;1;0;310;35.5;-8.5;35.5;-6;1.9;34.0690912;-7.25;0;0;0;"/><REC97003 IDX="970.03" index="310" content="970.03;310;D;BOGN;0;0;0;1;0;0;0;1;0;311;35.5;-6;32;-5;7;31.89309041;-11.99918355;0;0;0;"/><REC97003 IDX="970.03" index="311" content="970.03;311;D;BOGN;0;0;0;1;0;0;0;1;0;312;29;-4;32;-5;7;32.65638587;1.9691576;0;0;0;"/><REC97003 IDX="970.03" index="312" content="970.03;312;D;BOGN;0;0;0;1;0;0;0;1;0;313;29;-1.8;29;-4;1.2;29.47958315;-2.9;0;0;0;"/><REC97003 IDX="970.03" index="313" content="970.03;313;D;BOGN;0;0;0;1;0;0;0;1;0;314;35;-3;29;-1.8;5;31.22441089;-6.27794553;0;0;0;"/><REC97003 IDX="970.03" index="314" content="970.03;314;D;STRE;0;0;0;1;0;0;0;1;0;300;35;-3;36;-2;0;0;0;0;0;0;"/><REC97003 IDX="970.03" index="400" content="970.03;400;D;STRE;0;0;0;1;0;0;0;1;0;401;38;5;38;-10;0;0;0;0;0;0;"/><REC97003 IDX="970.03" index="401" content="970.03;401;D;STRE;0;0;0;1;0;0;0;1;0;402;38;-10;39.5;-10;0;0;0;0;0;0;"/><REC97003 IDX="970.03" index="402" content="970.03;402;D;STRE;0;0;0;1;0;0;0;1;0;403;39.5;-10;39.5;-3.5;0;0;0;0;0;0;"/><REC97003 IDX="970.03" index="403" content="970.03;403;D;BOGN;0;0;0;1;0;0;0;1;0;404;44;-3.5;39.5;-3.5;2.5;41.75;-4.58972474;0;0;0;"/><REC97003 IDX="970.03" index="404" content="970.03;404;D;STRE;0;0;0;1;0;0;0;1;0;405;44;-3.5;44;-10;0;0;0;0;0;0;"/><REC97003 IDX="970.03" index="405" content="970.03;405;D;STRE;0;0;0;1;0;0;0;1;0;406;44;-10;45.5;-10;0;0;0;0;0;0;"/><REC97003 IDX="970.03" index="406" content="970.03;406;D;STRE;0;0;0;1;0;0;0;1;0;407;45.5;-10;45.5;-3.5;0;0;0;0;0;0;"/><REC97003 IDX="970.03" index="407" content="970.03;407;D;BOGN;0;0;0;1;0;0;0;1;0;408;45.5;-3.5;39.5;-1.5;3.8;41.83366675;-4.49899975;0;0;0;"/><REC97003 IDX="970.03" index="408" content="970.03;408;D;STRE;0;0;0;1;0;0;0;1;0;409;39.5;-1.5;39.5;5;0;0;0;0;0;0;"/><REC97003 IDX="970.03" index="409" content="970.03;409;D;STRE;0;0;0;1;0;0;0;1;0;400;39.5;5;38;5;0;0;0;0;0;0;"/><REC97003 IDX="970.03" index="500" content="970.03;500;D;BOGN;0;0;0;1;0;0;0;1;0;501;50;-5;47;-6.5;3.5;49.87386317;-8.49772633;0;0;0;"/><REC97003 IDX="970.03" index="501" content="970.03;501;D;STRE;0;0;0;1;0;0;0;1;0;502;47;-6.5;47;-7.5;0;0;0;0;0;0;"/><REC97003 IDX="970.03" index="502" content="970.03;502;D;BOGN;0;0;0;1;0;0;0;1;0;503;47;-7.5;48;-9.5;2;48.9832397;-7.75838015;0;0;0;"/><REC97003 IDX="970.03" index="503" content="970.03;503;D;BOGN;0;0;0;1;0;0;0;1;0;504;48;-9.5;54.5;-9;5.5;50.91023364;-4.8330374;0;0;0;"/><REC97003 IDX="970.03" index="504" content="970.03;504;D;STRE;0;0;0;1;0;0;0;1;0;505;54.5;-9;55;-10;0;0;0;0;0;0;"/><REC97003 IDX="970.03" index="505" content="970.03;505;D;STRE;0;0;0;1;0;0;0;1;0;506;55;-10;56.5;-10;0;0;0;0;0;0;"/><REC97003 IDX="970.03" index="506" content="970.03;506;D;BOGN;0;0;0;1;0;0;0;1;0;507;56;-8.5;56.5;-10;2;57.99284251;-8.6690525;0;0;0;"/><REC97003 IDX="970.03" index="507" content="970.03;507;D;STRE;0;0;0;1;0;0;0;1;0;508;56;-8.5;56;-3;0;0;0;0;0;0;"/><REC97003 IDX="970.03" index="508" content="970.03;508;D;BOGN;0;0;0;1;0;0;0;1;0;509;56;-3;53;0;3;53;-3;0;0;0;"/><REC97003 IDX="970.03" index="509" content="970.03;509;D;STRE;0;0;0;1;0;0;0;1;0;510;53;0;49.5;0;0;0;0;0;0;0;"/><REC97003 IDX="970.03" index="510" content="970.03;510;D;BOGN;0;0;0;1;0;0;0;1;0;511;49.5;0;47;-3.5;4;50.99446618;-3.71033298;0;0;0;"/><REC97003 IDX="970.03" index="511" content="970.03;511;D;STRE;0;0;0;1;0;0;0;1;0;512;47;-3.5;48.5;-3.5;0;0;0;0;0;0;"/><REC97003 IDX="970.03" index="512" content="970.03;512;D;BOGN;0;0;0;1;0;0;0;1;0;513;50;-1.5;48.5;-3.5;2;50.4989996;-3.4367497;0;0;0;"/><REC97003 IDX="970.03" index="513" content="970.03;513;D;STRE;0;0;0;1;0;0;0;1;0;514;50;-1.5;53;-1.5;0;0;0;0;0;0;"/><REC97003 IDX="970.03" index="514" content="970.03;514;D;BOGN;0;0;0;1;0;0;0;1;0;515;54;-4;53;-1.5;1.5;52.88587039;-2.99565184;0;0;0;"/><REC97003 IDX="970.03" index="515" content="970.03;515;D;STRE;0;0;0;1;0;0;0;1;0;500;54;-4;50;-5;0;0;0;0;0;0;"/><REC97003 IDX="970.03" index="520" content="970.03;520;D;STRE;0;0;0;1;0;0;0;1;0;521;54.5;-5.5;50;-6.5;0;0;0;0;0;0;"/><REC97003 IDX="970.03" index="521" content="970.03;521;D;BOGN;0;0;0;1;0;0;0;1;0;522;50;-6.5;50;-9;1.3;50.35707142;-7.75;0;0;0;"/><REC97003 IDX="970.03" index="522" content="970.03;522;D;BOGN;0;0;0;1;0;0;0;1;0;523;50;-9;54;-8;4;51.16862976;-5.17451905;0;0;0;"/><REC97003 IDX="970.03" index="523" content="970.03;523;D;BOGN;0;0;0;1;0;0;0;1;0;520;54;-8;54.5;-5.5;5;49.50911806;-5.80182361;0;0;0;"/><REC97003 IDX="970.03" index="600" content="970.03;600;D;STRE;0;0;0;1;0;0;0;1;0;601;58;0;58;-7;0;0;0;0;0;0;"/><REC97003 IDX="970.03" index="601" content="970.03;601;D;BOGN;0;0;0;1;0;0;0;1;0;602;58;-7;61;-10;3;61;-7;0;0;0;"/><REC97003 IDX="970.03" index="602" content="970.03;602;D;STRE;0;0;0;1;0;0;0;1;0;603;61;-10;63;-10;0;0;0;0;0;0;"/><REC97003 IDX="970.03" index="603" content="970.03;603;D;BOGN;0;0;0;1;0;0;0;1;0;604;63;-10;65;-8.5;2;63.0632503;-8.001;0;0;0;"/><REC97003 IDX="970.03" index="604" content="970.03;604;D;STRE;0;0;0;1;0;0;0;1;0;605;65;-8.5;65.5;-10;0;0;0;0;0;0;"/><REC97003 IDX="970.03" index="605" content="970.03;605;D;STRE;0;0;0;1;0;0;0;1;0;606;65.5;-10;67;-10;0;0;0;0;0;0;"/><REC97003 IDX="970.03" index="606" content="970.03;606;D;BOGN;0;0;0;1;0;0;0;1;0;607;66.5;-8.5;67;-10;2;68.49284251;-8.6690525;0;0;0;"/><REC97003 IDX="970.03" index="607" content="970.03;607;D;STRE;0;0;0;1;0;0;0;1;0;608;66.5;-8.5;66.5;0;0;0;0;0;0;0;"/><REC97003 IDX="970.03" index="608" content="970.03;608;D;STRE;0;0;0;1;0;0;0;1;0;609;66.5;0;65;0;0;0;0;0;0;0;"/><REC97003 IDX="970.03" index="609" content="970.03;609;D;STRE;0;0;0;1;0;0;0;1;0;610;65;0;65;-7;0;0;0;0;0;0;"/><REC97003 IDX="970.03" index="610" content="970.03;610;D;BOGN;0;0;0;1;0;0;0;1;0;611;63;-8.5;65;-7;2;63.0632503;-6.5010004;0;0;0;"/><REC97003 IDX="970.03" index="611" content="970.03;611;D;STRE;0;0;0;1;0;0;0;1;0;612;63;-8.5;61.5;-8.5;0;0;0;0;0;0;"/><REC97003 IDX="970.03" index="612" content="970.03;612;D;BOGN;0;0;0;1;0;0;0;1;0;613;59.5;-7;61.5;-8.5;2;61.4367497;-6.5010004;0;0;0;"/><REC97003 IDX="970.03" index="613" content="970.03;613;D;STRE;0;0;0;1;0;0;0;1;0;614;59.5;-7;59.5;0;0;0;0;0;0;0;"/><REC97003 IDX="970.03" index="614" content="970.03;614;D;STRE;0;0;0;1;0;0;0;1;0;600;59.5;0;58;0;0;0;0;0;0;0;"/><REC97003 IDX="970.03" index="700" content="970.03;700;D;STRE;0;0;0;1;0;0;0;1;0;701;68.5;0;68.5;-12;0;0;0;0;0;0;"/><REC97003 IDX="970.03" index="701" content="970.03;701;D;STRE;0;0;0;1;0;0;0;1;0;702;68.5;-12;70;-12;0;0;0;0;0;0;"/><REC97003 IDX="970.03" index="702" content="970.03;702;D;STRE;0;0;0;1;0;0;0;1;0;703;70;-12;70;-9;0;0;0;0;0;0;"/><REC97003 IDX="970.03" index="703" content="970.03;703;D;BOGN;0;0;0;1;0;0;0;1;0;704;70;-9;74.5;-9;3;72.25;-7.01568652;0;0;0;"/><REC97003 IDX="970.03" index="704" content="970.03;704;D;BOGN;0;0;0;1;0;0;0;1;0;705;74.5;-9;74.5;-1;5;71.5;-5;0;0;0;"/><REC97003 IDX="970.03" index="705" content="970.03;705;D;BOGN;0;0;0;1;0;0;0;1;0;706;74.5;-1;70;-1;3;72.25;-2.98431348;0;0;0;"/><REC97003 IDX="970.03" index="706" content="970.03;706;D;STRE;0;0;0;1;0;0;0;1;0;707;70;-1;70;0;0;0;0;0;0;0;"/><REC97003 IDX="970.03" index="707" content="970.03;707;D;STRE;0;0;0;1;0;0;0;1;0;700;70;0;68.5;0;0;0;0;0;0;0;"/><REC97003 IDX="970.03" index="720" content="970.03;720;D;BOGN;0;0;0;1;0;0;0;1;0;721;74;-2.5;71;-2.5;2.5;72.5;-4.5;0;0;0;"/><REC97003 IDX="970.03" index="721" content="970.03;721;D;BOGN;0;0;0;1;0;0;0;1;0;722;71;-2.5;71;-7.5;4;74.122499;-5;0;0;0;"/><REC97003 IDX="970.03" index="722" content="970.03;722;D;BOGN;0;0;0;1;0;0;0;1;0;723;71;-7.5;74;-7.5;2.5;72.5;-5.5;0;0;0;"/><REC97003 IDX="970.03" index="723" content="970.03;723;D;BOGN;0;0;0;1;0;0;0;1;0;720;74;-7.5;74;-2.5;4;70.877501;-5;0;0;0;"/><REC97003 IDX="970.03" index="800" content="970.03;800;D;STRE;0;0;0;1;0;0;0;1;0;801;78;-1.5;78;-8;0;0;0;0;0;0;"/><REC97003 IDX="970.03" index="801" content="970.03;801;D;BOGN;0;0;0;1;0;0;0;1;0;802;78;-8;80;-10;2;80;-8;0;0;0;"/><REC97003 IDX="970.03" index="802" content="970.03;802;D;STRE;0;0;0;1;0;0;0;1;0;803;80;-10;82;-10;0;0;0;0;0;0;"/><REC97003 IDX="970.03" index="803" content="970.03;803;D;BOGN;0;0;0;1;0;0;0;1;0;804;82;-10;83;-9;1;82;-9;0;0;0;"/><REC97003 IDX="970.03" index="804" content="970.03;804;D;STRE;0;0;0;1;0;0;0;1;0;805;83;-9;83;-7.5;0;0;0;0;0;0;"/><REC97003 IDX="970.03" index="805" content="970.03;805;D;BOGN;0;0;0;1;0;0;0;1;0;806;82;-8.5;83;-7.5;1;82;-7.5;0;0;0;"/><REC97003 IDX="970.03" index="806" content="970.03;806;D;STRE;0;0;0;1;0;0;0;1;0;807;82;-8.5;80.5;-8.5;0;0;0;0;0;0;"/><REC97003 IDX="970.03" index="807" content="970.03;807;D;BOGN;0;0;0;1;0;0;0;1;0;808;79.5;-7.5;80.5;-8.5;1;80.5;-7.5;0;0;0;"/><REC97003 IDX="970.03" index="808" content="970.03;808;D;STRE;0;0;0;1;0;0;0;1;0;809;79.5;-7.5;79.5;-1.5;0;0;0;0;0;0;"/><REC97003 IDX="970.03" index="809" content="970.03;809;D;STRE;0;0;0;1;0;0;0;1;0;810;79.5;-1.5;82;-1.5;0;0;0;0;0;0;"/><REC97003 IDX="970.03" index="810" content="970.03;810;D;STRE;0;0;0;1;0;0;0;1;0;811;82;-1.5;82;0;0;0;0;0;0;0;"/><REC97003 IDX="970.03" index="811" content="970.03;811;D;STRE;0;0;0;1;0;0;0;1;0;812;82;0;79.5;0;0;0;0;0;0;0;"/><REC97003 IDX="970.03" index="812" content="970.03;812;D;STRE;0;0;0;1;0;0;0;1;0;813;79.5;0;79.5;5;0;0;0;0;0;0;"/><REC97003 IDX="970.03" index="813" content="970.03;813;D;STRE;0;0;0;1;0;0;0;1;0;814;79.5;5;78;5;0;0;0;0;0;0;"/><REC97003 IDX="970.03" index="814" content="970.03;814;D;STRE;0;0;0;1;0;0;0;1;0;815;78;5;78;0;0;0;0;0;0;0;"/><REC97003 IDX="970.03" index="815" content="970.03;815;D;STRE;0;0;0;1;0;0;0;1;0;816;78;0;76.5;0;0;0;0;0;0;0;"/><REC97003 IDX="970.03" index="816" content="970.03;816;D;STRE;0;0;0;1;0;0;0;1;0;817;76.5;0;76.5;-1.5;0;0;0;0;0;0;"/><REC97003 IDX="970.03" index="817" content="970.03;817;D;STRE;0;0;0;1;0;0;0;1;0;800;76.5;-1.5;78;-1.5;0;0;0;0;0;0;"/></RECORDS_970_03><RECORDS_970_04><REC97004 IDX="970.04" index="2" content="970.04;2;1;0;0;1;0.671;0.145;0.141;1;1;0;0;1;64;0;0;0;1;"/></RECORDS_970_04></REC970><REC970 IDX="970" index="46201102" content="970;46201102;WTC-OB 20/25/30/35 A W-PEA / H-O;0;QUAD;840;-1533;0;0;1;0;-1;0;0;1583;1680;1230;0;0;0;0;0;0;0;0;"><RECORDS_970_01><REC97001 IDX="970.01" index="1" content="970.01;1;1;E;RK;MUFF;228T1;DN;40;0;0;-137;-84;1225;0;0;1;-1;0;0;0;0;0;0;0;0;"/><REC97001 IDX="970.01" index="3" content="970.01;3;3;A;VK;MUFF;13T1;DN;40;0;0;-262;-84;1225;0;0;1;-1;0;0;0;0;0;0;0;0;"/><REC97001 IDX="970.01" index="5" content="970.01;5;5;A;AA;MUFF;1298;DN;125;0;30;181;-162;1196.5;0;0;1;0;-1;0;0;0;0;0;0;0;"/><REC97001 IDX="970.01" index="6" content="970.01;6;6;E;VL;MUFF;1298;DN;80;0;30;181;-162;1220;0;0;1;0;-1;0;0;0;0;0;0;0;"/><REC97001 IDX="970.01" index="7" content="970.01;7;7;E;OEL;MUFF;1298;DN;12;0;15;280;-50;1225;0;0;1;0;1;0;0;0;0;0;0;0;"/><REC97001 IDX="970.01" index="8" content="970.01;8;8;A;ST;NIPP;228T1;DN;25;0;20;0;-50;1227;0;0;1;0;1;0;0;0;0;0;0;0;"/><REC97001 IDX="970.01" index="10" content="970.01;10;10;A;VS;NIPP;228T1;DN;25;0;18;358;-46;987;1;0;0;0;1;0;0;0;0;0;0;0;"/><REC97001 IDX="970.01" index="11" content="970.01;11;11;E;RS;NIPP;228T1;DN;25;0;18;358;-46;328;1;0;0;0;1;0;0;0;0;0;0;0;"/><REC97001 IDX="970.01" index="12" content="970.01;12;12;A;VS;NIPP;228T1;DN;25;0;18;-358;-46;987;-1;0;0;0;1;0;0;0;0;0;0;0;"/><REC97001 IDX="970.01" index="13" content="970.01;13;13;E;RS;NIPP;228T1;DN;25;0;18;-358;-46;328;-1;0;0;0;1;0;0;0;0;0;0;0;"/><REC97001 IDX="970.01" index="14" content="970.01;14;14;A;VSL;NIPP;228T1;DN;20;0;14;-360;-46;169;-1;0;0;0;1;0;0;0;0;0;0;0;"/></RECORDS_970_01><RECORDS_970_02><REC97002 IDX="970.02" index="1" content="970.02;1;G;RFER;0;0;0;1;0;0;0;1;0;0;0;0;520;0;0;0;0;0;0;0;"/><REC97002 IDX="970.02" index="65" content="970.02;65;G;ZYLI;340;-46;987;1;0;0;0;1;0;18;16.8;0;0;0;0;0;0;0;0;3;"/><REC97002 IDX="970.02" index="67" content="970.02;67;G;ZYLI;340;-46;328;1;0;0;0;1;0;18;16.8;0;0;0;0;0;0;0;0;3;"/><REC97002 IDX="970.02" index="68" content="970.02;68;G;WIED;0;-92;0;-1;0;0;0;-1;0;1;0;0;0;0;0;0;0;0;0;0;65;67;"/><REC97002 IDX="970.02" index="72" content="970.02;72;G;ZYLI;-340;-46;169;-1;0;0;0;1;0;20;13.4;0;0;0;0;0;0;0;0;4;"/><REC97002 IDX="970.02" index="2" content="970.02;2;G;RFER;195;-732;1115;1;0;0;0;0;1;0;0;0;2;0;0;0;0;0;0;0;"/></RECORDS_970_02><RECORDS_970_03><REC97003 IDX="970.03" index="1" content="970.03;1;G;RFER;0;0;0;1;0;0;0;1;0;0;0;0;520;0;0;0;0;0;0;0;"/><REC97003 IDX="970.03" index="2" content="970.03;2;G;RFER;195;-732;1115;1;0;0;0;0;1;0;0;0;2;0;0;0;0;0;0;0;"/><REC97003 IDX="970.03" index="34" content="970.03;34;G;TRAN;335;-600;50;0;1;0;0;0;1;0;0;1;5;900;0;0;0;0;0;1;1123;1119;"/><REC97003 IDX="970.03" index="35" content="970.03;35;G;TRAN;-340;-600;50;0;1;0;0;0;1;0;0;1;5;900;0;0;0;0;0;1;1122;1118;"/><REC97003 IDX="970.03" index="65" content="970.03;65;G;ZYLI;300;-46;987;1;0;0;0;1;0;50;16.8;0;0;0;0;0;0;0;0;3;"/><REC97003 IDX="970.03" index="66" content="970.03;66;G;VKNT;350;-46;987;1;0;0;0;1;0;12;18;6;0;0;0;0;0;0;0;3;"/><REC97003 IDX="970.03" index="67" content="970.03;67;G;ZYLI;300;-46;328;1;0;0;0;1;0;50;16.8;0;0;0;0;0;0;0;0;3;"/><REC97003 IDX="970.03" index="68" content="970.03;68;G;VKNT;350;-46;328;1;0;0;0;1;0;12;18;6;0;0;0;0;0;0;0;3;"/><REC97003 IDX="970.03" index="69" content="970.03;69;G;WIED;0;-92;0;-1;0;0;0;-1;0;1;0;0;0;0;0;0;0;0;0;0;65;66;67;68;"/><REC97003 IDX="970.03" index="70" content="970.03;70;G;ZYLI;-280;-46;250;0;0;-1;0;1;0;61;13.4;0;0;0;0;0;0;0;0;4;"/><REC97003 IDX="970.03" index="71" content="970.03;71;G;TOBO;-280;-46;189;0;0;-1;-1;0;0;90;20;13.4;0;0;0;0;0;0;0;4;"/><REC97003 IDX="970.03" index="72" content="970.03;72;G;ZYLI;-300;-46;169;-1;0;0;0;1;0;50;13.4;0;0;0;0;0;0;0;0;4;"/><REC97003 IDX="970.03" index="73" content="970.03;73;G;VKNT;-350;-46;169;-1;0;0;0;1;0;14;15;6;0;0;0;0;0;0;0;3;"/><REC97003 IDX="970.03" index="750" content="970.03;750;D;STRE;0;0;0;1;0;0;0;1;0;751;20;-50;20;0;0;0;0;0;0;0;"/><REC97003 IDX="970.03" index="751" content="970.03;751;D;BOGN;0;0;0;1;0;0;0;1;0;752;20;0;-20;0;20;0;0;0;0;0;"/><REC97003 IDX="970.03" index="752" content="970.03;752;D;STRE;0;0;0;1;0;0;0;1;0;753;-20;0;-20;-50;0;0;0;0;0;0;"/><REC97003 IDX="970.03" index="753" content="970.03;753;D;STRE;0;0;0;1;0;0;0;1;0;750;-20;-50;20;-50;0;0;0;0;0;0;"/><REC97003 IDX="970.03" index="900" content="970.03;900;D;STRE;0;0;0;1;0;0;0;1;0;901;0;0;0;1016.5;0;0;0;0;0;0;"/><REC97003 IDX="970.03" index="901" content="970.03;901;D;STRE;0;0;0;1;0;0;0;1;0;902;0;1016.5;600;1016.5;0;0;0;0;0;0;"/><REC97003 IDX="970.03" index="902" content="970.03;902;D;STRE;0;0;0;1;0;0;0;1;0;903;600;1016.5;600;298;0;0;0;0;0;0;"/><REC97003 IDX="970.03" index="903" content="970.03;903;D;STRE;0;0;0;1;0;0;0;1;0;904;600;298;554;298;0;0;0;0;0;0;"/><REC97003 IDX="970.03" index="904" content="970.03;904;D;BOGN;0;0;0;1;0;0;0;1;0;905;554;298;554;258;20;554;278;0;0;0;"/><REC97003 IDX="970.03" index="905" content="970.03;905;D;STRE;0;0;0;1;0;0;0;1;0;906;554;258;600;258;0;0;0;0;0;0;"/><REC97003 IDX="970.03" index="906" content="970.03;906;D;STRE;0;0;0;1;0;0;0;1;0;907;600;258;600;139;0;0;0;0;0;0;"/><REC97003 IDX="970.03" index="907" content="970.03;907;D;STRE;0;0;0;1;0;0;0;1;0;908;600;139;554;139;0;0;0;0;0;0;"/><REC97003 IDX="970.03" index="908" content="970.03;908;D;BOGN;0;0;0;1;0;0;0;1;0;909;554;139;554;99;20;554;119;0;0;0;"/><REC97003 IDX="970.03" index="909" content="970.03;909;D;STRE;0;0;0;1;0;0;0;1;0;910;554;99;600;99;0;0;0;0;0;0;"/><REC97003 IDX="970.03" index="910" content="970.03;910;D;STRE;0;0;0;1;0;0;0;1;0;911;600;99;600;0;0;0;0;0;0;0;"/><REC97003 IDX="970.03" index="911" content="970.03;911;D;STRE;0;0;0;1;0;0;0;1;0;900;600;0;0;0;0;0;0;0;0;0;"/><REC97003 IDX="970.03" index="1118" content="970.03;1118;H;TRAN;-345;-46;987;0;0;1;0;-1;0;0;0;1;20;750;0;0;0;0;0;0;"/><REC97003 IDX="970.03" index="1119" content="970.03;1119;H;ZYLI;325;-46;70;1;0;0;0;1;0;20;17;0;0;0;0;0;0;0;0;0;"/><REC97003 IDX="970.03" index="1122" content="970.03;1122;H;ZYLI;-345;-46;70;1;0;0;0;1;0;20;17;0;0;0;0;0;0;0;0;0;"/><REC97003 IDX="970.03" index="1123" content="970.03;1123;H;TRAN;345;-46;987;0;0;1;0;-1;0;0;0;1;-20;750;0;0;0;0;0;0;"/></RECORDS_970_03><RECORDS_970_04><REC97004 IDX="970.04" index="1" content="970.04;1;0.867;0.871;0.831;1;0.867;0.871;0.831;1;0.867;0.871;0.831;1;64;0;0;0;1;"/><REC97004 IDX="970.04" index="3" content="970.04;3;0.5;0.5;0.4;1;0.502;0.502;0.502;1;0.6;0.6;0.2;1;64;0;0;0;1;"/><REC97004 IDX="970.04" index="4" content="970.04;4;0.8118;0.8118;0.8118;1;0.7451;0.7451;0.7451;1;0.8745;0.8745;0.8745;1;48;0;0;0;1;"/></RECORDS_970_04></REC970></RECORDS_970></REC010></pData>

## geometry (parser evidence)
native form markers: Sweep x2
no freeform markers — native parametric forms only
